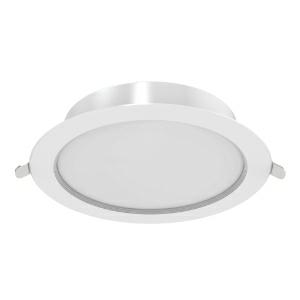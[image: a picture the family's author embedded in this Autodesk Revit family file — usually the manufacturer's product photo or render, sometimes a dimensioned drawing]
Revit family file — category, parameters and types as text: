
# Revit family: leddownlightco-e_rd100-9w-830_540001290900
name_source: partatom
category: Leuchten
revit_build: Autodesk Revit 2016 (Build: 20190508_0715(x64)
units: mm (PartAtom-declared; Revit-internal decimal feet)

## family parameters
Basisbauteil = Fläche
Beim Laden mit Abzugskörper schneiden = Nein
Bemaßung runder Anschluss = Durchmesser verwenden
Gemeinsam genutzt = Nein
Lichtquelle = Nein
Raumberechnungspunkt = Nein
Teiletyp = Normal

## types (1)
- LEDDownlightCo-E Rd100-9W-830 (1 x LED, 810 lm)
    Approval mark = CE
    Beschreibung = Stylish and compact LED downlight. Sturdy full metal housing. Integrated driver for easier installation. Low height of only 35mm. IP44 on light emitting side.
    CIE Flux Codes = 52 82 97 100 100
    Control Gear = Electronic ballast
    Height = 0 mm  [stored 0 ft]
    Hersteller = OPPLE
    Lamp Light Flux = 810 lm
    Lamp count = 1
    Lampe = 1 x LED
    Length = 100 mm  [stored 0.328084 ft]
    Luminous efficacy = 90 lm/W
    ModVariant = Nein
    Modell = 540001290900
    Mounting Place = Ceiling
    Mounting Type = Recessed
    Number of Poles = 1
    OnlyDefault = Ja
    Power Factor = 1
    Product Name = LEDDownlightCo-E Rd100-9W-830
    Product group = Downlight Compact
    ProductGroupID = 406
    Protection Class = Protection class II
    Protection Degree = IP 44
    RLX_Detail_Level = 1
    RlxData = <blob elided: 104781 chars, md5=4737a4f4>
    Scheinlast = 9 VA
    Socket = socket
    Standby Power = 0 W
    System Light Flux = 810 lm
    System Power = 9 W
    Typenbild = 540001290900.jpg
    Typenkommentare = Product without accessories
    URL = http://relux.com
    VarID = ---
    Voltage = 230 V
    Voltage Range = 220-240 V
    Vorgabe-Ansicht = 1800 mm
    Weight = 0.00 kg
    Width = 100 mm  [stored 0.328084 ft]

note: [stored X ft] marks values corroborated as IEEE doubles in the binary element streams (Revit-internal decimal feet)

## geometry (parser evidence)
native form markers: Sweep x9
no freeform markers — native parametric forms only
